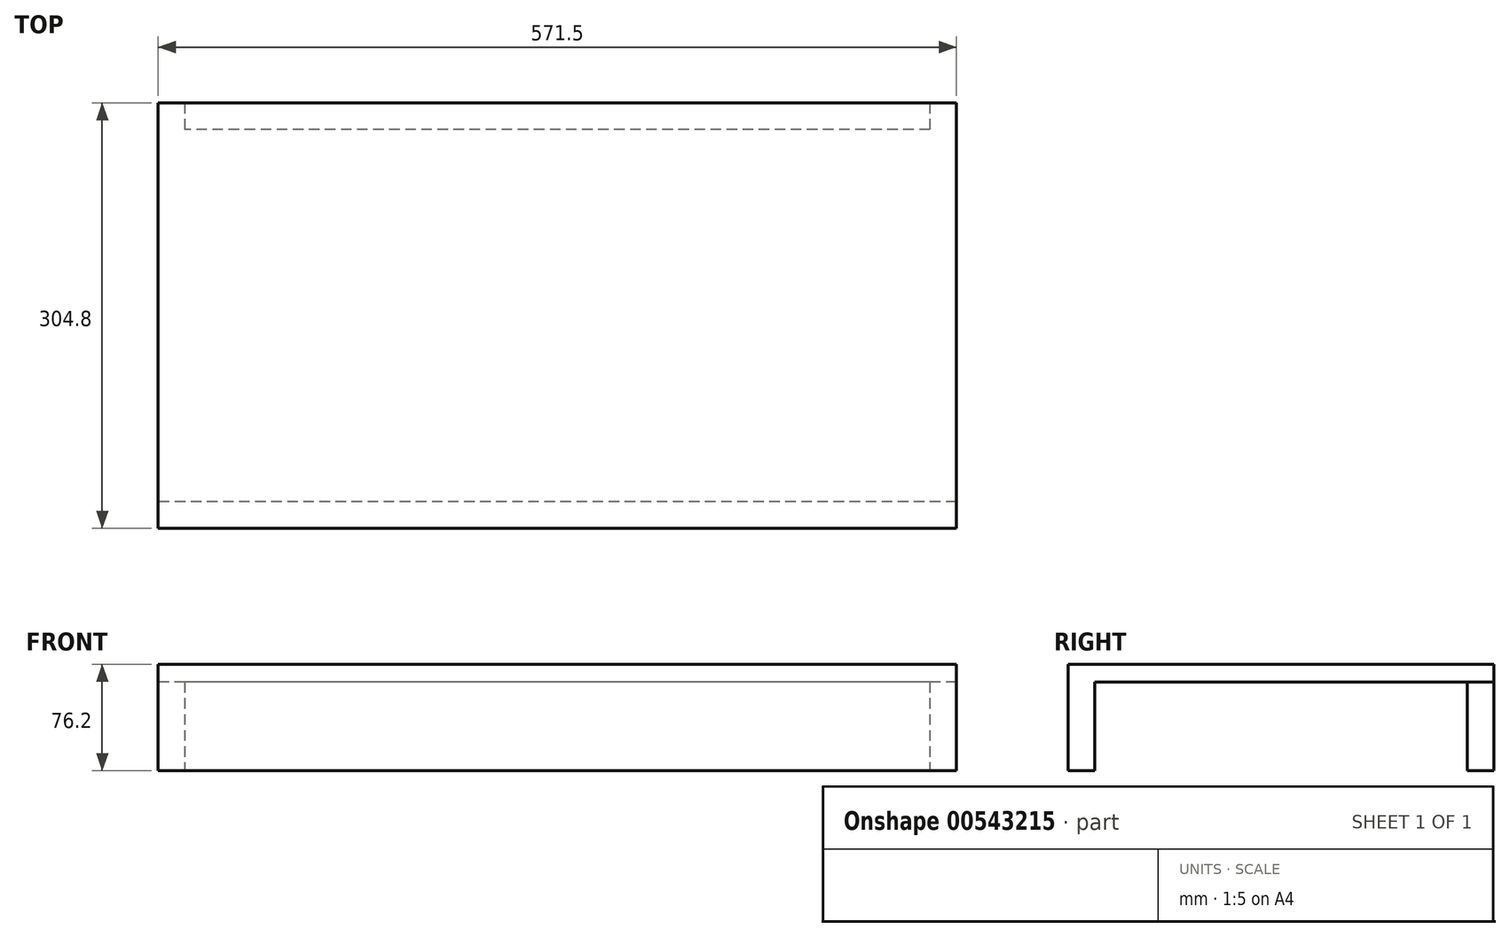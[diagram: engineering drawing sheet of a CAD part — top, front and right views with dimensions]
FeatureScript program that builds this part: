
annotation { "Feature Type Name" : "Feature", "Feature Type Description" : "" }
export const myFeature = defineFeature(function(context is Context, id is Id, definition is map)
    precondition{}
    {
        {
            var Q0;
            Q0=qCreatedBy(makeId("Top.planeOp"),FACE);
            var sketch = newSketch(context, id + "F0", { "sketchPlane" : qUnion([Q0])});
            skLineSegment(sketch, "E0.bottom", {"start": v(285.75, 152.4) * mm, "end": v(-285.75, 152.4) * mm});
            skLineSegment(sketch, "E0.top", {"start": v(285.75, -152.4) * mm, "end": v(-285.75, -152.4) * mm});
            skLineSegment(sketch, "E0.left", {"start": v(285.75, 152.4) * mm, "end": v(285.75, -152.4) * mm});
            skLineSegment(sketch, "E0.right", {"start": v(-285.75, 152.4) * mm, "end": v(-285.75, -152.4) * mm});
            skPoint(sketch, "E0.middle", {"position": v(0, 0) * mm});
            skSolve(sketch);
        }
        {
            var Q0;
            Q0 = qSketchRegion(id + "F0", true);
            extrude(context, id + "F1", {"entities" : qUnion([Q0]), "depth" : 12.7 * mm, "offsetDistance" : 25.4 * mm});
        }
        {
            var Q0;
            Q0=qCreatedBy(makeId("Right.planeOp"),FACE);
            var sketch = newSketch(context, id + "F2", { "sketchPlane" : qUnion([Q0])});
            skLineSegment(sketch, "E1.bottom", {"start": v(-152.4, 0) * mm, "end": v(-133.35, 0) * mm});
            skLineSegment(sketch, "E1.top", {"start": v(-152.4, -63.5) * mm, "end": v(-133.35, -63.5) * mm});
            skLineSegment(sketch, "E1.left", {"start": v(-152.4, 0) * mm, "end": v(-152.4, -63.5) * mm});
            skLineSegment(sketch, "E1.right", {"start": v(-133.35, 0) * mm, "end": v(-133.35, -63.5) * mm});
            skSolve(sketch);
        }
        {
            var Q0;
            Q0 = qSketchRegion(id + "F2", true);
            extrude(context, id + "F3", {"entities" : qUnion([Q0]), "operationType" : NewBodyOperationType.ADD, "endBound" : BoundingType.SYMMETRIC, "depth" : 571.5 * mm, "offsetDistance" : 25.4 * mm});
        }
        {
            var Q0;
            Q0=qCreatedBy(makeId("Right.planeOp"),FACE);
            var sketch = newSketch(context, id + "F4", { "sketchPlane" : qUnion([Q0])});
            skLineSegment(sketch, "E2.bottom", {"start": v(152.4, 0) * mm, "end": v(133.35, 0) * mm});
            skLineSegment(sketch, "E2.top", {"start": v(152.4, -63.5) * mm, "end": v(133.35, -63.5) * mm});
            skLineSegment(sketch, "E2.left", {"start": v(152.4, 0) * mm, "end": v(152.4, -63.5) * mm});
            skLineSegment(sketch, "E2.right", {"start": v(133.35, 0) * mm, "end": v(133.35, -63.5) * mm});
            skSolve(sketch);
        }
        {
            var Q0;
            Q0 = qSketchRegion(id + "F4", true);
            extrude(context, id + "F5", {"entities" : qUnion([Q0]), "operationType" : NewBodyOperationType.ADD, "endBound" : BoundingType.SYMMETRIC, "depth" : 533.4 * mm, "offsetDistance" : 25.4 * mm});
        }
    });
